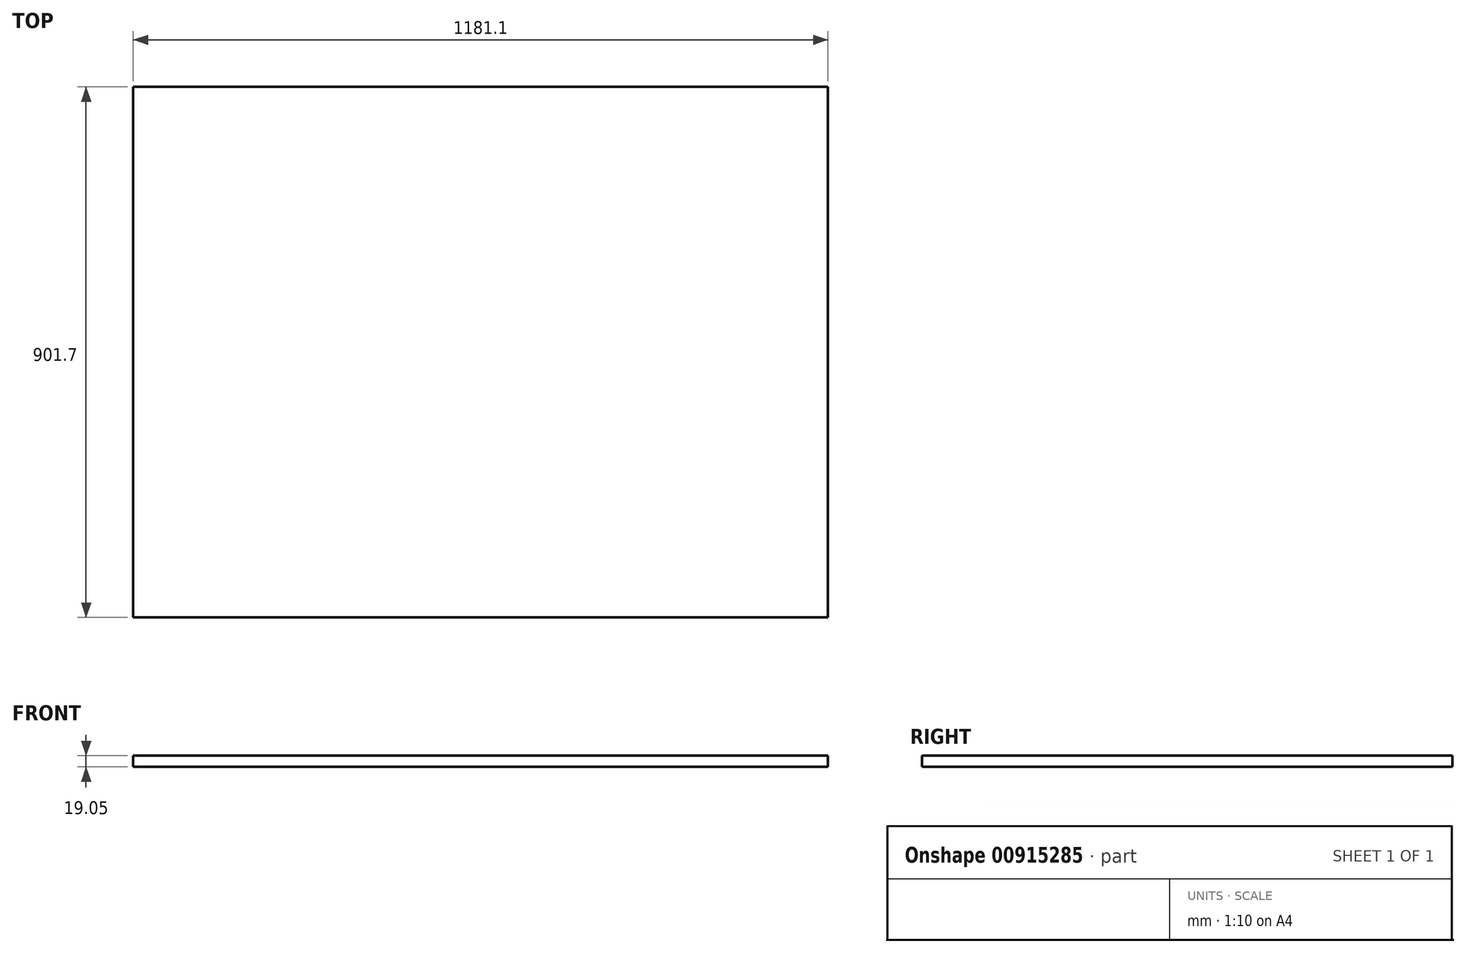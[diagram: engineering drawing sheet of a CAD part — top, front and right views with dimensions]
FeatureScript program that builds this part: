
annotation { "Feature Type Name" : "Feature", "Feature Type Description" : "" }
export const myFeature = defineFeature(function(context is Context, id is Id, definition is map)
    precondition{}
    {
        {
            var Q0;
            Q0=qCreatedBy(makeId("Top.planeOp"),FACE);
            var sketch = newSketch(context, id + "F0", { "sketchPlane" : qUnion([Q0])});
            skLineSegment(sketch, "E0.bottom", {"start": v(590.55, 450.85) * mm, "end": v(-590.55, 450.85) * mm});
            skLineSegment(sketch, "E0.top", {"start": v(590.55, -450.85) * mm, "end": v(-590.55, -450.85) * mm});
            skLineSegment(sketch, "E0.left", {"start": v(590.55, 450.85) * mm, "end": v(590.55, -450.85) * mm});
            skLineSegment(sketch, "E0.right", {"start": v(-590.55, 450.85) * mm, "end": v(-590.55, -450.85) * mm});
            skPoint(sketch, "E0.middle", {"position": v(0, 0) * mm});
            skSolve(sketch);
        }
        {
            var Q0;
            Q0=makeQuery(id+"F0.imprint","IMPRINT",FACE,{"disambiguationData":[TD([[makeQuery(id+"F0.imprint","IMPRINT",EDGE,{"derivedFrom":sQuery(id+"F0.wireOp",EDGE,"E0.bottom")}),1.0]])]});
            extrude(context, id + "F1", {"entities" : qUnion([Q0]), "depth" : 19.05 * mm, "offsetDistance" : 25.4 * mm});
        }
    });
